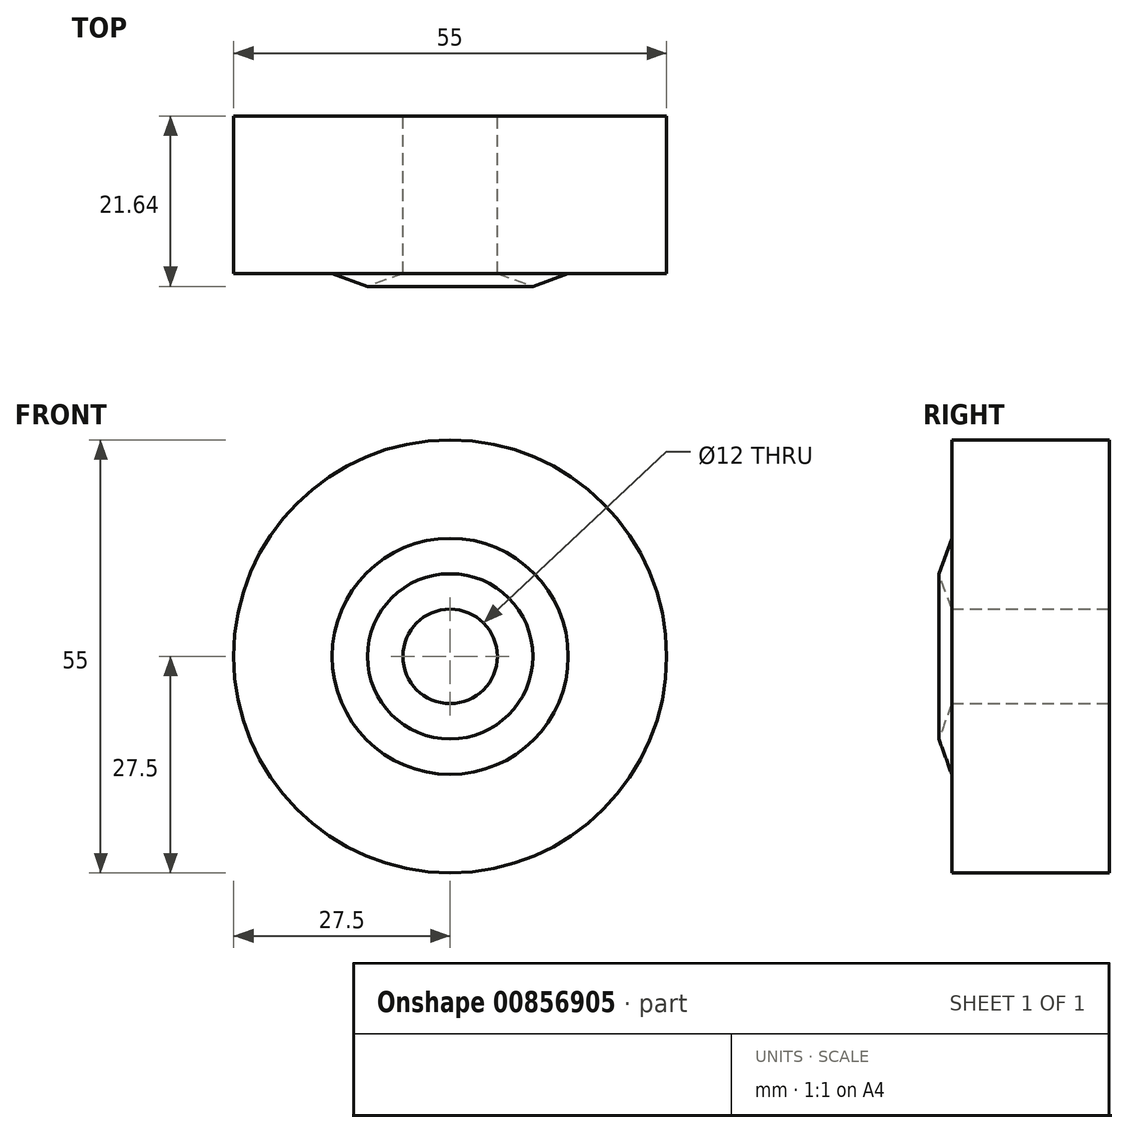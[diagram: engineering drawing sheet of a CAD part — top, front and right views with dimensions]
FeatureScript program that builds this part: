
annotation { "Feature Type Name" : "Feature", "Feature Type Description" : "" }
export const myFeature = defineFeature(function(context is Context, id is Id, definition is map)
    precondition{}
    {
        {
            var Q0;
            Q0=qCreatedBy(makeId("Front.planeOp"),FACE);
            var sketch = newSketch(context, id + "F0", { "sketchPlane" : qUnion([Q0])});
            skCircle(sketch, "E0", {"center": v(0, 0) * mm, "radius": 27.5 * mm});
            skCircle(sketch, "E1", {"center": v(0, 0) * mm, "radius": 15 * mm});
            skCircle(sketch, "E2", {"center": v(0, 0) * mm, "radius": 6 * mm});
            skSolve(sketch);
        }
        {
            var Q0;
            Q0=makeQuery(id+"F0.imprint","IMPRINT",FACE,{"disambiguationData":[TD([[makeQuery(id+"F0.imprint","IMPRINT",EDGE,{"derivedFrom":sQuery(id+"F0.wireOp",EDGE,"E1")}),1.0]])]});
            var Q1;
            Q1=makeQuery(id+"F0.imprint","IMPRINT",FACE,{"disambiguationData":[TD([[makeQuery(id+"F0.imprint","IMPRINT",EDGE,{"derivedFrom":sQuery(id+"F0.wireOp",EDGE,"E0")}),1.0]])]});
            extrude(context, id + "F1", {"entities" : qUnion([Q0, Q1]), "depth" : 20 * mm, "offsetDistance" : 25 * mm});
        }
        {
            var Q0;
            Q0=makeQuery(id+"F1.opExtrude","CAP_FACE",FACE,{"disambiguationData":[OSD([sQuery(id+"F0.wireOp",EDGE,"E0"),sQuery(id+"F0.wireOp",EDGE,"E2")])],"isStart":false});
            var sketch = newSketch(context, id + "F2", { "sketchPlane" : qUnion([Q0])});
            skCircle(sketch, "E3", {"center": v(0, 0) * mm, "radius": 15 * mm});
            skSolve(sketch);
        }
        {
            var Q0;
            Q0=makeQuery(id+"F2.imprint","IMPRINT",FACE,{"disambiguationData":[TD([[makeQuery(id+"F2.imprint","IMPRINT",EDGE,{"derivedFrom":sQuery(id+"F2.wireOp",EDGE,"E3")}),1.0]])]});
            extrude(context, id + "F3", {"entities" : qUnion([Q0]), "operationType" : NewBodyOperationType.ADD, "depth" : 10 * mm, "offsetDistance" : 25 * mm, "hasDraft" : true, "draftAngle" : 70 * degree, "draftPullDirection" : true});
        }
    });
